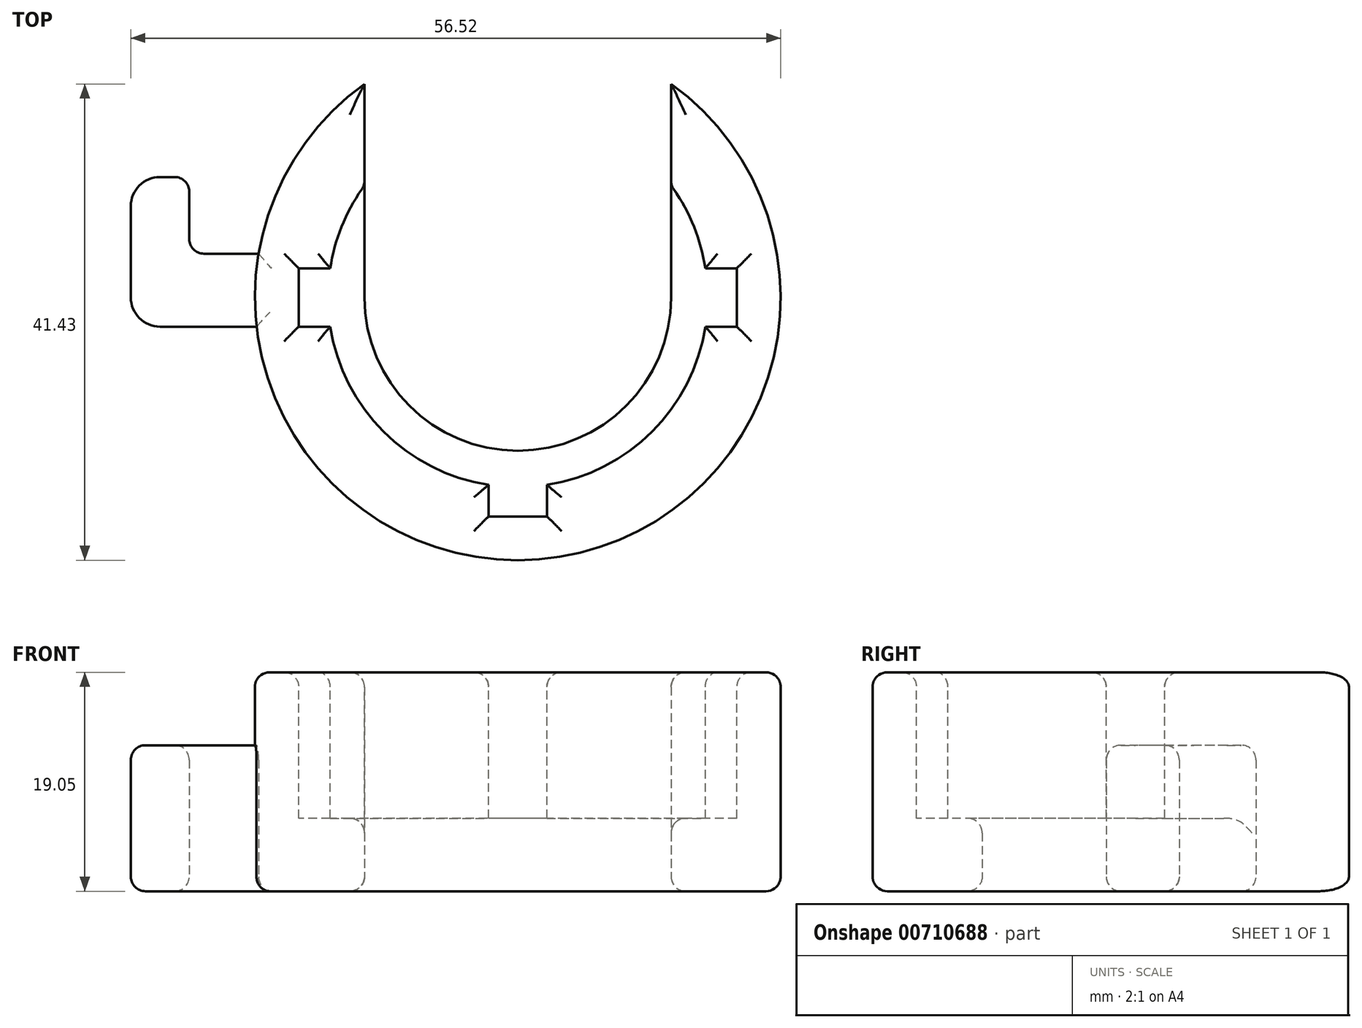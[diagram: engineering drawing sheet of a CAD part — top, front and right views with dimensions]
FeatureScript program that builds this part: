
annotation { "Feature Type Name" : "Feature", "Feature Type Description" : "" }
export const myFeature = defineFeature(function(context is Context, id is Id, definition is map)
    precondition{}
    {
        {
            var Q0;
            Q0=qCreatedBy(makeId("Top.planeOp"),FACE);
            var sketch = newSketch(context, id + "F0", { "sketchPlane" : qUnion([Q0])});
            skCircle(sketch, "E0", {"center": v(0, 0) * mm, "radius": 16.51 * mm});
            skCircle(sketch, "E1", {"center": v(0, 0) * mm, "radius": 22.86 * mm});
            skSolve(sketch);
        }
        {
            var Q0;
            Q0=makeQuery(id+"F0.imprint","IMPRINT",FACE,{"disambiguationData":[TD([[makeQuery(id+"F0.imprint","IMPRINT",EDGE,{"derivedFrom":sQuery(id+"F0.wireOp",EDGE,"E0")}),-1.0]])]});
            extrude(context, id + "F1", {"entities" : qUnion([Q0]), "depth" : 12.7 * mm, "offsetDistance" : 25.4 * mm});
        }
        {
            var Q0;
            Q0=makeQuery(id+"F1.opExtrude","CAP_FACE",FACE,{"disambiguationData":[OSD([sQuery(id+"F0.wireOp",EDGE,"E0"),sQuery(id+"F0.wireOp",EDGE,"E1")])],"isStart":true});
            var sketch = newSketch(context, id + "F2", { "sketchPlane" : qUnion([Q0])});
            skCircle(sketch, "E2", {"center": v(0, 0) * mm, "radius": 13.34 * mm});
            skSolve(sketch);
        }
        {
            var Q0;
            Q0=makeQuery(id+"F2.imprint","IMPRINT",FACE,{"disambiguationData":[TD([[makeQuery(id+"F2.imprint","IMPRINT",EDGE,{"derivedFrom":sQuery(id+"F2.wireOp",EDGE,"E2")}),-1.0]])]});
            var Q1;
            Q1=makeQuery(id+"F2.imprint","IMPRINT",FACE,{"disambiguationData":[TD([[makeQuery(id+"F2.imprint","IMPRINT",EDGE,{"derivedFrom":makeQuery(id+"F1.opExtrude","CAP_EDGE",EDGE,{"disambiguationData":[OSD([sQuery(id+"F0.wireOp",EDGE,"E0")])],"isStart":true})}),1.0]])]});
            var Q2;
            Q2=makeQuery(id+"F2.imprint","IMPRINT",FACE,{"disambiguationData":[TD([[makeQuery(id+"F2.imprint","IMPRINT",EDGE,{"derivedFrom":sQuery(id+"F2.wireOp",EDGE,"E2")}),1.0]])]});
            extrude(context, id + "F3", {"entities" : qUnion([Q0, Q1, Q2]), "operationType" : NewBodyOperationType.ADD, "depth" : 6.35 * mm, "offsetDistance" : 25.4 * mm});
        }
        {
            var Q0;
            Q0=makeQuery(id+"F3.opExtrude","CAP_FACE",FACE,{"disambiguationData":[OSD([sQuery(id+"F0.wireOp",EDGE,"E1")])],"isStart":false});
            var sketch = newSketch(context, id + "F4", { "sketchPlane" : qUnion([Q0])});
            skCircle(sketch, "E3", {"center": v(0, 0) * mm, "radius": 13.33 * mm});
            skSolve(sketch);
        }
        {
            var Q0;
            Q0=makeQuery(id+"F4.imprint","IMPRINT",FACE,{"disambiguationData":[TD([[makeQuery(id+"F4.imprint","IMPRINT",EDGE,{"derivedFrom":sQuery(id+"F4.wireOp",EDGE,"E3")}),1.0]])]});
            extrude(context, id + "F5", {"entities" : qUnion([Q0]), "operationType" : NewBodyOperationType.REMOVE, "endBound" : BoundingType.THROUGH_ALL, "oppositeDirection" : true, "depth" : 25.4 * mm, "offsetDistance" : 25.4 * mm});
        }
        {
            var Q0;
            Q0=makeQuery(id+"F3.opExtrude","CAP_FACE",FACE,{"disambiguationData":[OSD([sQuery(id+"F0.wireOp",EDGE,"E1")])],"isStart":false});
            var sketch = newSketch(context, id + "F6", { "sketchPlane" : qUnion([Q0])});
            skLineSegment(sketch, "E4.bottom", {"start": v(-13.33, 0) * mm, "end": v(13.33, 0) * mm});
            skLineSegment(sketch, "E4.top", {"start": v(-13.33, -45.66) * mm, "end": v(13.34, -45.66) * mm});
            skLineSegment(sketch, "E4.left", {"start": v(-13.34, 0) * mm, "end": v(-13.33, -45.66) * mm});
            skLineSegment(sketch, "E4.right", {"start": v(13.33, 0) * mm, "end": v(13.34, -45.66) * mm});
            skSolve(sketch);
        }
        {
            var Q0;
            {var subQ0=sQuery(id+"F6.wireOp",EDGE,"E4.left");var subQ4=makeQuery(id+"F3.opExtrude","CAP_EDGE",EDGE,{"disambiguationData":[OSD([sQuery(id+"F0.wireOp",EDGE,"E1")])],"isStart":false});var subQ5=makeQuery(id+"F6.imprint","INTERSECT",VERTEX,{"derivedFrom":[subQ4,subQ0]});Q0=makeQuery(id+"F6.imprint","IMPRINT",FACE,{"disambiguationData":[TD([[makeQuery(id+"F6.imprint","IMPRINT",EDGE,{"disambiguationData":[TD([[subQ5,1.0]])],"derivedFrom":subQ4}),-1.0]])]});}
            extrude(context, id + "F7", {"entities" : qUnion([Q0]), "operationType" : NewBodyOperationType.REMOVE, "endBound" : BoundingType.THROUGH_ALL, "oppositeDirection" : true, "depth" : 25.4 * mm, "offsetDistance" : 25.4 * mm});
        }
        {
            var Q0;
            Q0=makeQuery(id+"F1.opExtrude","CAP_FACE",FACE,{"disambiguationData":[OSD([sQuery(id+"F0.wireOp",EDGE,"E0"),sQuery(id+"F0.wireOp",EDGE,"E1")])],"isStart":false});
            var sketch = newSketch(context, id + "F8", { "sketchPlane" : qUnion([Q0])});
            skLineSegment(sketch, "E5.bottom", {"start": v(19.05, 2.54) * mm, "end": v(-19.05, 2.54) * mm});
            skLineSegment(sketch, "E5.top", {"start": v(19.05, -2.54) * mm, "end": v(-19.05, -2.54) * mm});
            skLineSegment(sketch, "E5.left", {"start": v(19.05, 2.54) * mm, "end": v(19.05, -2.54) * mm});
            skLineSegment(sketch, "E5.right", {"start": v(-19.05, 2.54) * mm, "end": v(-19.05, -2.54) * mm});
            skPoint(sketch, "E5.middle", {"position": v(0, 0) * mm});
            skLineSegment(sketch, "E6.bottom", {"start": v(2.54, 19.05) * mm, "end": v(-2.54, 19.05) * mm});
            skLineSegment(sketch, "E6.top", {"start": v(2.54, -19.05) * mm, "end": v(-2.54, -19.05) * mm});
            skLineSegment(sketch, "E6.left", {"start": v(2.54, 19.05) * mm, "end": v(2.54, -19.05) * mm});
            skLineSegment(sketch, "E6.right", {"start": v(-2.54, 19.05) * mm, "end": v(-2.54, -19.05) * mm});
            skSolve(sketch);
        }
        {
            var Q0;
            {var subQ0=sQuery(id+"F8.wireOp",EDGE,"E5.right");Q0=makeQuery(id+"F8.imprint","IMPRINT",FACE,{"disambiguationData":[TD([[makeQuery(id+"F8.imprint","IMPRINT",EDGE,{"derivedFrom":subQ0}),1.0]])]});}
            var Q1;
            {var subQ0=sQuery(id+"F8.wireOp",EDGE,"E6.top");Q1=makeQuery(id+"F8.imprint","IMPRINT",FACE,{"disambiguationData":[TD([[makeQuery(id+"F8.imprint","IMPRINT",EDGE,{"derivedFrom":subQ0}),-1.0]])]});}
            var Q2;
            {var subQ0=sQuery(id+"F8.wireOp",EDGE,"E5.left");Q2=makeQuery(id+"F8.imprint","IMPRINT",FACE,{"disambiguationData":[TD([[makeQuery(id+"F8.imprint","IMPRINT",EDGE,{"derivedFrom":subQ0}),-1.0]])]});}
            var Q3;
            Q3=makeQuery(id+"F3.opExtrude","CAP_FACE",FACE,{"disambiguationData":[OSD([sQuery(id+"F0.wireOp",EDGE,"E1")])],"isStart":true});
            extrude(context, id + "F9", {"entities" : qUnion([Q0, Q1, Q2]), "operationType" : NewBodyOperationType.REMOVE, "endBound" : BoundingType.UP_TO_SURFACE, "oppositeDirection" : true, "depth" : 25.4 * mm, "endBoundEntityFace" : qUnion([Q3]), "offsetDistance" : 25.4 * mm});
        }
        {
            var Q0;
            Q0=makeQuery(id+"F7.boolean.opBoolean","COPY",EDGE,{"derivedFrom":makeQuery(id+"F7.opExtrude","SWEPT_EDGE",EDGE,{"disambiguationData":[OSD([sQuery(id+"F0.wireOp",EDGE,"E1"),sQuery(id+"F6.wireOp",EDGE,"E4.right")])]})});
            var Q1;
            Q1=makeQuery(id+"F7.boolean.opBoolean","COPY",EDGE,{"derivedFrom":makeQuery(id+"F7.opExtrude","SWEPT_EDGE",EDGE,{"disambiguationData":[OSD([sQuery(id+"F0.wireOp",EDGE,"E1"),sQuery(id+"F6.wireOp",EDGE,"E4.left")])]})});
            var Q2;
            Q2=makeQuery(id+"F1.opExtrude","CAP_EDGE",EDGE,{"disambiguationData":[OSD([sQuery(id+"F0.wireOp",EDGE,"E1")])],"isStart":false});
            var Q3;
            {var subQ0=sQuery(id+"F0.wireOp",EDGE,"E0");var subQ2=makeQuery(id+"F1.opExtrude","CAP_EDGE",EDGE,{"disambiguationData":[OSD([subQ0])],"isStart":false});Q3=makeQuery(id+"F9.boolean.opBoolean","SPLIT",EDGE,{"disambiguationData":[TD([makeQuery(id+"F7.boolean.opBoolean","COPY",FACE,{"derivedFrom":makeQuery(id+"F7.opExtrude","SWEPT_FACE",FACE,{"disambiguationData":[OSD([sQuery(id+"F6.wireOp",EDGE,"E4.right")])]})})])],"derivedFrom":subQ2});}
            var Q4;
            {var subQ0=sQuery(id+"F8.wireOp",EDGE,"E5.bottom");Q4=makeQuery(id+"F9.boolean.opBoolean","COPY",EDGE,{"derivedFrom":makeQuery(id+"F9.opExtrude","CAP_EDGE",EDGE,{"disambiguationData":[OSD([subQ0]),TDD([makeQuery(id+"F8.imprint","IMPRINT",EDGE,{"disambiguationData":[TD([[makeQuery(id+"F8.imprint","INTERSECT",VERTEX,{"derivedFrom":[subQ0,sQuery(id+"F8.wireOp",EDGE,"E5.left")]}),-1.0]])],"derivedFrom":subQ0})])],"isStart":true})});}
            var Q5;
            Q5=makeQuery(id+"F9.boolean.opBoolean","COPY",EDGE,{"derivedFrom":makeQuery(id+"F9.opExtrude","CAP_EDGE",EDGE,{"disambiguationData":[OSD([sQuery(id+"F8.wireOp",EDGE,"E5.left")])],"isStart":true})});
            var Q6;
            {var subQ0=sQuery(id+"F8.wireOp",EDGE,"E5.top");Q6=makeQuery(id+"F9.boolean.opBoolean","COPY",EDGE,{"derivedFrom":makeQuery(id+"F9.opExtrude","CAP_EDGE",EDGE,{"disambiguationData":[OSD([subQ0]),TDD([makeQuery(id+"F8.imprint","IMPRINT",EDGE,{"disambiguationData":[TD([[makeQuery(id+"F8.imprint","INTERSECT",VERTEX,{"derivedFrom":[subQ0,sQuery(id+"F8.wireOp",EDGE,"E5.left")]}),-1.0]])],"derivedFrom":subQ0})])],"isStart":true})});}
            var Q7;
            {var subQ0=sQuery(id+"F0.wireOp",EDGE,"E0");var subQ2=makeQuery(id+"F1.opExtrude","CAP_EDGE",EDGE,{"disambiguationData":[OSD([subQ0])],"isStart":false});Q7=makeQuery(id+"F9.boolean.opBoolean","SPLIT",EDGE,{"disambiguationData":[TD([makeQuery(id+"F9.opExtrude","SWEPT_FACE",FACE,{"disambiguationData":[OSD([sQuery(id+"F8.wireOp",EDGE,"E6.left")])]})])],"derivedFrom":subQ2});}
            var Q8;
            Q8=makeQuery(id+"F1.opExtrude","CAP_FACE",FACE,{"disambiguationData":[OSD([sQuery(id+"F0.wireOp",EDGE,"E0"),sQuery(id+"F0.wireOp",EDGE,"E1")])],"isStart":false});
            var Q9;
            Q9=makeQuery(id+"F7.boolean.opBoolean","INTERSECT",EDGE,{"derivedFrom":[makeQuery(id+"F3.opExtrude","CAP_FACE",FACE,{"disambiguationData":[OSD([sQuery(id+"F0.wireOp",EDGE,"E1")])],"isStart":true}),makeQuery(id+"F7.opExtrude","SWEPT_FACE",FACE,{"disambiguationData":[OSD([sQuery(id+"F6.wireOp",EDGE,"E4.left")])]})]});
            var Q10;
            Q10=makeQuery(id+"F7.boolean.opBoolean","INTERSECT",EDGE,{"derivedFrom":[makeQuery(id+"F1.opExtrude","SWEPT_FACE",FACE,{"disambiguationData":[OSD([sQuery(id+"F0.wireOp",EDGE,"E0")])]}),makeQuery(id+"F7.opExtrude","SWEPT_FACE",FACE,{"disambiguationData":[OSD([sQuery(id+"F6.wireOp",EDGE,"E4.left")])]})]});
            var Q11;
            Q11=makeQuery(id+"F7.boolean.opBoolean","INTERSECT",EDGE,{"derivedFrom":[makeQuery(id+"F1.opExtrude","SWEPT_FACE",FACE,{"disambiguationData":[OSD([sQuery(id+"F0.wireOp",EDGE,"E0")])]}),makeQuery(id+"F7.opExtrude","SWEPT_FACE",FACE,{"disambiguationData":[OSD([sQuery(id+"F6.wireOp",EDGE,"E4.right")])]})]});
            fillet(context, id + "F10", {"entities" : qUnion([Q0, Q1, Q2, Q3, Q4, Q5, Q6, Q7, Q8, Q9, Q10, Q11]), "radius" : 1.27 * mm, "tangentPropagation" : true, "allowEdgeOverflow" : false});
        }
        {
            var Q0;
            Q0=makeQuery(id+"F3.opExtrude","CAP_FACE",FACE,{"disambiguationData":[OSD([sQuery(id+"F0.wireOp",EDGE,"E1")])],"isStart":false});
            var sketch = newSketch(context, id + "F11", { "sketchPlane" : qUnion([Q0])});
            skLineSegment(sketch, "E7.bottom", {"start": v(-13.33, -10.48) * mm, "end": v(-31.11, -10.48) * mm});
            skLineSegment(sketch, "E7.top", {"start": v(-13.34, 2.54) * mm, "end": v(-31.11, 2.54) * mm});
            skLineSegment(sketch, "E7.left", {"start": v(-13.34, -10.48) * mm, "end": v(-13.34, 2.54) * mm});
            skLineSegment(sketch, "E7.right", {"start": v(-33.65, -7.94) * mm, "end": v(-33.65, 0) * mm});
            skPoint(sketch, "E8.visualSharp", {"position": v(-33.65, 2.54) * mm});
            skArc(sketch, "E8.filletArc", {"start": v(-31.11, 2.54) * mm, "mid": v(-32.91, 1.8) * mm, "end": v(-33.65, 0) * mm});
            skPoint(sketch, "E9.visualSharp", {"position": v(-33.65, -10.48) * mm});
            skArc(sketch, "E9.filletArc", {"start": v(-33.65, -7.94) * mm, "mid": v(-32.91, -9.73) * mm, "end": v(-31.11, -10.48) * mm});
            skLineSegment(sketch, "E10.bottom", {"start": v(-28.57, -10.48) * mm, "end": v(-19.68, -10.48) * mm});
            skLineSegment(sketch, "E10.top", {"start": v(-27.3, -3.81) * mm, "end": v(-20.96, -3.8) * mm});
            skLineSegment(sketch, "E10.left", {"start": v(-28.57, -10.48) * mm, "end": v(-28.57, -5.08) * mm});
            skLineSegment(sketch, "E10.right", {"start": v(-19.68, -10.48) * mm, "end": v(-19.69, -5.08) * mm});
            skPoint(sketch, "E11.visualSharp", {"position": v(-28.57, -3.81) * mm});
            skArc(sketch, "E11.filletArc", {"start": v(-27.3, -3.81) * mm, "mid": v(-28.2, -4.18) * mm, "end": v(-28.57, -5.08) * mm});
            skPoint(sketch, "E12.visualSharp", {"position": v(-19.69, -3.8) * mm});
            skArc(sketch, "E12.filletArc", {"start": v(-19.69, -5.08) * mm, "mid": v(-20.06, -4.18) * mm, "end": v(-20.96, -3.81) * mm});
            skLineSegment(sketch, "E13.MirrorCS", {"start": v(13.33, -10.48) * mm, "end": v(31.11, -10.48) * mm});
            skLineSegment(sketch, "E14.MirrorCS", {"start": v(13.34, -10.48) * mm, "end": v(13.34, 2.54) * mm});
            skLineSegment(sketch, "E15.MirrorCS", {"start": v(13.34, 2.54) * mm, "end": v(31.11, 2.54) * mm});
            skArc(sketch, "E16.MirrorCS", {"start": v(31.11, 2.54) * mm, "mid": v(32.91, 1.8) * mm, "end": v(33.65, 0) * mm});
            skLineSegment(sketch, "E17.MirrorCS", {"start": v(33.65, -7.94) * mm, "end": v(33.65, 0) * mm});
            skArc(sketch, "E18.MirrorCS", {"start": v(33.65, -7.94) * mm, "mid": v(32.91, -9.73) * mm, "end": v(31.11, -10.48) * mm});
            skLineSegment(sketch, "E19.MirrorCS", {"start": v(28.57, -10.48) * mm, "end": v(28.57, -5.08) * mm});
            skPoint(sketch, "E20.MirrorP", {"position": v(28.57, -3.81) * mm});
            skArc(sketch, "E21.MirrorCS", {"start": v(27.3, -3.81) * mm, "mid": v(28.2, -4.18) * mm, "end": v(28.57, -5.08) * mm});
            skLineSegment(sketch, "E22.MirrorCS", {"start": v(27.3, -3.8) * mm, "end": v(20.96, -3.8) * mm});
            skArc(sketch, "E23.MirrorCS", {"start": v(19.69, -5.08) * mm, "mid": v(20.06, -4.18) * mm, "end": v(20.96, -3.81) * mm});
            skLineSegment(sketch, "E24.MirrorCS", {"start": v(19.69, -10.48) * mm, "end": v(19.69, -5.08) * mm});
            skSolve(sketch);
        }
        {
            var Q0;
            Q0=makeQuery(id+"F11.imprint","IMPRINT",FACE,{"disambiguationData":[TD([[makeQuery(id+"F11.imprint","IMPRINT",EDGE,{"derivedFrom":sQuery(id+"F11.wireOp",EDGE,"E7.right")}),-1.0]])]});
            var Q1;
            {var subQ6=sQuery(id+"F11.wireOp",EDGE,"E16.MirrorCS");Q1=makeQuery(id+"F11.imprint","IMPRINT",FACE,{"disambiguationData":[TD([[makeQuery(id+"F11.imprint","IMPRINT",EDGE,{"derivedFrom":subQ6}),-1.0]])]});}
            extrude(context, id + "F12", {"entities" : qUnion([Q0, Q1]), "operationType" : NewBodyOperationType.ADD, "oppositeDirection" : true, "depth" : 12.7 * mm, "offsetDistance" : 25.4 * mm});
        }
        {
            var Q0;
            Q0=makeQuery(id+"F12.opExtrude","CAP_EDGE",EDGE,{"disambiguationData":[OSD([sQuery(id+"F11.wireOp",EDGE,"E10.top")])],"isStart":false});
            var Q1;
            {var subQ0=sQuery(id+"F11.wireOp",EDGE,"E7.bottom");Q1=makeQuery(id+"F12.opExtrude","CAP_EDGE",EDGE,{"disambiguationData":[OSD([subQ0]),TDD([makeQuery(id+"F11.imprint","IMPRINT",EDGE,{"disambiguationData":[TD([[makeQuery(id+"F11.imprint","INTERSECT",VERTEX,{"derivedFrom":[subQ0,sQuery(id+"F11.wireOp",EDGE,"E9.filletArc")]}),1.0]])],"derivedFrom":subQ0})])],"isStart":false});}
            var Q2;
            {var subQ0=sQuery(id+"F0.wireOp",EDGE,"E1");Q2=makeQuery(id+"F12.boolean.opBoolean","MERGE",FACE,{"derivedFrom":[makeQuery(id+"F3.opExtrude","CAP_FACE",FACE,{"disambiguationData":[OSD([subQ0])],"isStart":false}),makeQuery(id+"F12.opExtrude","CAP_FACE",FACE,{"disambiguationData":[OSD([subQ0,sQuery(id+"F11.wireOp",EDGE,"E7.bottom"),sQuery(id+"F11.wireOp",EDGE,"E7.top"),sQuery(id+"F11.wireOp",EDGE,"E7.right"),sQuery(id+"F11.wireOp",EDGE,"E8.filletArc"),sQuery(id+"F11.wireOp",EDGE,"E9.filletArc"),sQuery(id+"F11.wireOp",EDGE,"E10.top"),sQuery(id+"F11.wireOp",EDGE,"E10.left"),sQuery(id+"F11.wireOp",EDGE,"E10.right"),sQuery(id+"F11.wireOp",EDGE,"E11.filletArc"),sQuery(id+"F11.wireOp",EDGE,"E12.filletArc")])],"isStart":true}),makeQuery(id+"F12.opExtrude","CAP_FACE",FACE,{"disambiguationData":[OSD([subQ0,sQuery(id+"F11.wireOp",EDGE,"E13.MirrorCS"),sQuery(id+"F11.wireOp",EDGE,"E15.MirrorCS"),sQuery(id+"F11.wireOp",EDGE,"E16.MirrorCS"),sQuery(id+"F11.wireOp",EDGE,"E17.MirrorCS"),sQuery(id+"F11.wireOp",EDGE,"E18.MirrorCS"),sQuery(id+"F11.wireOp",EDGE,"E19.MirrorCS"),sQuery(id+"F11.wireOp",EDGE,"E21.MirrorCS"),sQuery(id+"F11.wireOp",EDGE,"E22.MirrorCS"),sQuery(id+"F11.wireOp",EDGE,"E23.MirrorCS"),sQuery(id+"F11.wireOp",EDGE,"E24.MirrorCS")])],"isStart":true})]});}
            var Q3;
            Q3=makeQuery(id+"F12.opExtrude","CAP_EDGE",EDGE,{"disambiguationData":[OSD([sQuery(id+"F11.wireOp",EDGE,"E22.MirrorCS")])],"isStart":false});
            var Q4;
            {var subQ0=sQuery(id+"F11.wireOp",EDGE,"E13.MirrorCS");Q4=makeQuery(id+"F12.opExtrude","CAP_EDGE",EDGE,{"disambiguationData":[OSD([subQ0]),TDD([makeQuery(id+"F11.imprint","IMPRINT",EDGE,{"disambiguationData":[TD([[makeQuery(id+"F11.imprint","INTERSECT",VERTEX,{"derivedFrom":[subQ0,sQuery(id+"F11.wireOp",EDGE,"E18.MirrorCS")]}),1.0]])],"derivedFrom":subQ0})])],"isStart":false});}
            var Q5;
            Q5=makeQuery(id+"F12.opExtrude","SWEPT_EDGE",EDGE,{"disambiguationData":[OSD([sQuery(id+"F11.wireOp",EDGE,"E7.bottom"),sQuery(id+"F11.wireOp",EDGE,"E10.bottom"),sQuery(id+"F11.wireOp",EDGE,"E10.left")])]});
            var Q6;
            Q6=makeQuery(id+"F12.opExtrude","SWEPT_EDGE",EDGE,{"disambiguationData":[OSD([sQuery(id+"F11.wireOp",EDGE,"E13.MirrorCS"),sQuery(id+"F11.wireOp",EDGE,"E19.MirrorCS")])]});
            fillet(context, id + "F13", {"entities" : qUnion([Q0, Q1, Q2, Q3, Q4, Q5, Q6]), "radius" : 1.27 * mm, "tangentPropagation" : true, "allowEdgeOverflow" : false});
        }
    });
